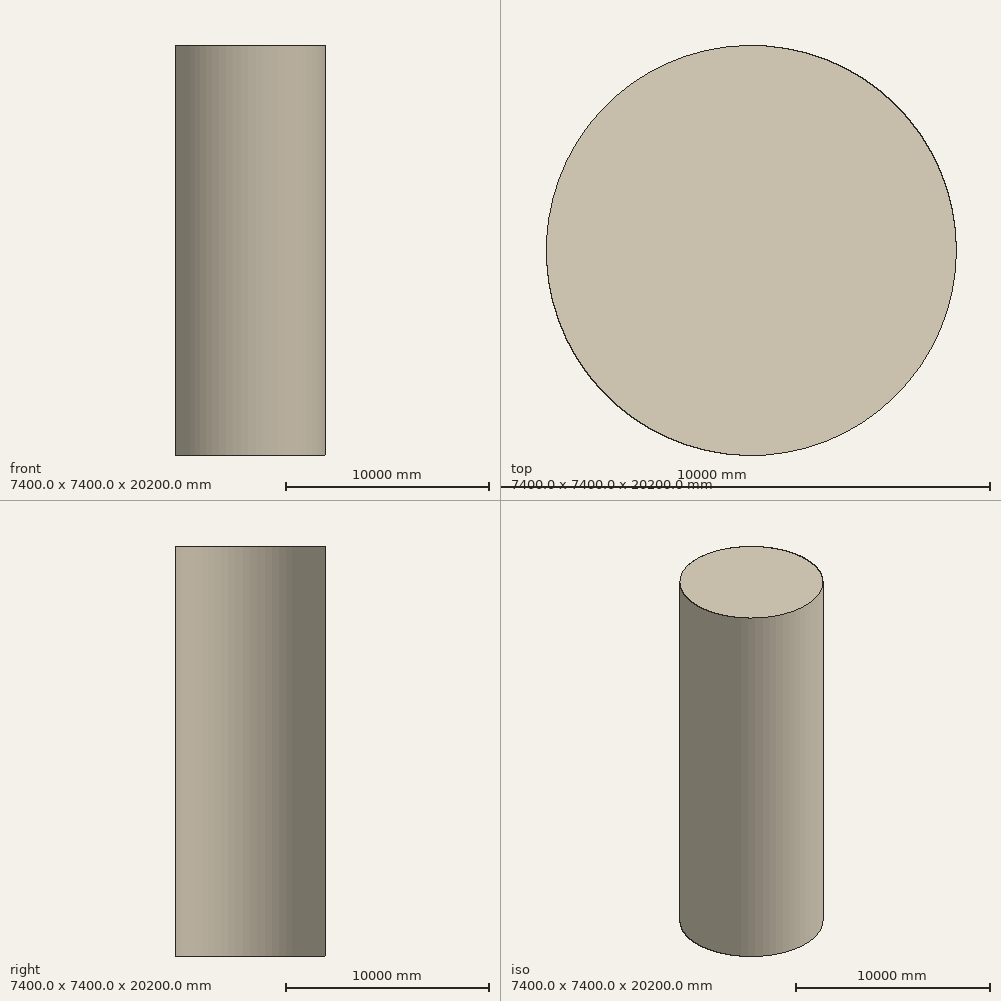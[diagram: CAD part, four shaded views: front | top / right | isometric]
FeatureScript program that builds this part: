
annotation { "Feature Type Name" : "Feature", "Feature Type Description" : "" }
export const myFeature = defineFeature(function(context is Context, id is Id, definition is map)
    precondition{}
    {
        {
            var Q0;
            Q0=qCreatedBy(makeId("Top.planeOp"),FACE);
            var sketch = newSketch(context, id + "F0", { "sketchPlane" : qUnion([Q0])});
            skCircle(sketch, "E0", {"center": v(0, 0) * mm, "radius": 3700 * mm});
            skSolve(sketch);
        }
        {
            var Q0;
            {var subQ0=sQuery(id+"F0.wireOp",EDGE,"E0");var subQ4=makeQuery(id+"F0.imprint","INTERSECT",VERTEX,{"derivedFrom":[subQ0,sQuery(id+"F0.wireOp",EDGE,"LX5xFx08-Gr3r-SUbO-4MDW-dQZDL7cysQ94")]});Q0=makeQuery(id+"F0.imprint","IMPRINT",FACE,{"disambiguationData":[TD([[makeQuery(id+"F0.imprint","IMPRINT",EDGE,{"disambiguationData":[TD([[subQ4,1.0]])],"derivedFrom":subQ0}),1.0]])]});}
            extrude(context, id + "F1", {"entities" : qUnion([Q0]), "depth" : 20200 * mm, "offsetDistance" : 25.4 * mm});
        }
    });
